FCSTD DOCUMENT  (FreeCAD 0.18R4 (GitTag))
Label: commutationSystem1
License: All rights reserved
LicenseURL: http://en.wikipedia.org/wiki/All_rights_reserved
objects: Sketcher::SketchObject×5, PartDesign::Body×2, Spreadsheet::Sheet×1
note: 7 computed .brp shape members not serialized (recipe doc carries the construction recipe); baked Part::Feature solids carry a one-line shape summary decoded from their .brp

FEATURE [Spreadsheet::Sheet] Spreadsheet  label="Variables"
  cells = A2=segmentNumber; B2(segmentNumber)=6; A3=outerDiameter; B3(outerDiameter)=30; D3=Calc Value; A4=innerDiameter; B4(innerDiameter)=24.7; D4=Input Value; A5=length; B5(length)=5; A6=segmentAngle; B6(segmentAngle)==360 / segmentNumber; A7=brushWidth; B7(brushWidth)=6; A8=brushHeight; B8(brushHeight)=2; A9=brushLength; B9(brushLength)=5; A10=commutatorDisplacementAngle; B10(commutatorDisplacementAngle)=6; A11=statorStackLength; B11(statorStackLength)=20; A12=stackDistance; B12(stackDistance)=10; A13=commutatorIsolationThickness; B13(commutatorIsolationThickness)=0.5
FEATURE [Sketcher::SketchObject] Sketch003  label="CommutatorSegment"
  MapMode = 5
  expr: Constraints[20] = Variables.commutatorIsolationThickness / 2
  expr: Constraints[13] = Variables.segmentAngle / 2 + Variables.commutatorDisplacementAngle
  expr: Constraints[12] = Variables.segmentAngle
  expr: Constraints[3] = Variables.outerDiameter
  expr: Placement.Rotation.Angle = 0
  expr: Constraints[2] = Variables.innerDiameter
  sketch-geometry (12):
    g0: Circle [constr] CenterX=0 CenterY=0 CenterZ=0 NormalX=0 NormalY=0 NormalZ=1 AngleXU=0 Radius=12.35
    g1: Circle [constr] CenterX=0 CenterY=0 CenterZ=0 NormalX=0 NormalY=0 NormalZ=1 AngleXU=0 Radius=15
    g2: LineSegment [constr] StartX=11.2823 StartY=-5.0232 StartZ=0 EndX=13.7032 EndY=-6.10105 EndZ=0
    g3: LineSegment [constr] StartX=9.99136 StartY=7.25915 StartZ=0 EndX=12.1353 EndY=8.81678 EndZ=0
    g4: LineSegment [constr] StartX=0 StartY=0 StartZ=0 EndX=11.2823 EndY=-5.0232 EndZ=0
    g5: LineSegment [constr] StartX=0 StartY=0 StartZ=0 EndX=9.99136 EndY=7.25915 EndZ=0
    g6: LineSegment StartX=10.1363 StartY=7.05541 StartZ=0 EndX=12.2805 EndY=8.6133 EndZ=0
    g7: LineSegment [constr] StartX=9.98931 StartY=7.25766 StartZ=0 EndX=10.1363 EndY=7.05541 EndZ=0
    g8: LineSegment StartX=11.3817 StartY=-4.79378 StartZ=0 EndX=13.803 EndY=-5.87182 EndZ=0
    g9: LineSegment [constr] StartX=11.3817 StartY=-4.79378 StartZ=0 EndX=11.28 EndY=-5.02217 EndZ=0
    g10: ArcOfCircle CenterX=0 CenterY=0 CenterZ=0 NormalX=0 NormalY=0 NormalZ=1 AngleXU=0 Radius=12.35 StartAngle=5.88455 EndAngle=6.89126
    g11: ArcOfCircle CenterX=0 CenterY=0 CenterZ=0 NormalX=0 NormalY=0 NormalZ=1 AngleXU=0 Radius=15 StartAngle=5.88097 EndAngle=6.89484
  constraints (34):
    c: Coincident(g0,g-1)
    c: Coincident(g1,g0)
    c: Diameter(g0) = 24.7
    c: Diameter(g1) = 30
    c: PointOnObject(g2,g0)
    c: PointOnObject(g2,g1)
    c: Coincident(g4,g-1)
    c: Coincident(g4,g2)
    c: Coincident(g5,g4)
    c: Coincident(g5,g3)
    c: Parallel(g4,g2)
    c: Parallel(g5,g3)
    c: Angle(g4,g5) = 1.0472
    c: Angle(g-1,g5) = 0.628319
    c: PointOnObject(g3,g1)
    c: PointOnObject(g3,g0)
    c: Parallel(g3,g6)
    c: PointOnObject(g7,g3)
    c: Coincident(g7,g6)
    c: Angle(g6,g7) = 1.5708
    c: Distance(g7) = 0.25
    c: PointOnObject(g8,g0)
    c: Parallel(g8,g2)
    c: Coincident(g9,g8)
    c: PointOnObject(g9,g4)
    c: Angle(g9,g8) = 1.5708
    c: Equal(g9,g7)
    c: PointOnObject(g8,g1)
    c: Coincident(g10,g-1)
    c: Coincident(g10,g8)
    c: Coincident(g10,g6)
    c: Coincident(g11,g10)
    c: Coincident(g11,g8)
    c: Coincident(g11,g6)
FEATURE [Sketcher::SketchObject] Sketch  label="BoundingBox"
  MapMode = 5
  Support = -> [XY_Plane]
  expr: Constraints[8] = Variables.outerDiameter
  sketch-geometry (6):
    g0: LineSegment StartX=-15 StartY=-15 StartZ=0 EndX=15 EndY=-15 EndZ=0
    g1: LineSegment StartX=15 StartY=-15 StartZ=0 EndX=15 EndY=15 EndZ=0
    g2: LineSegment StartX=15 StartY=15 StartZ=0 EndX=-15 EndY=15 EndZ=0
    g3: LineSegment StartX=-15 StartY=15 StartZ=0 EndX=-15 EndY=-15 EndZ=0
    g4: LineSegment [constr] StartX=-15 StartY=-15 StartZ=0 EndX=15 EndY=15 EndZ=0
    g5: GeomPoint X=0 Y=0 Z=0
  constraints (14):
    c: Coincident(g0,g1)
    c: Coincident(g1,g2)
    c: Coincident(g2,g3)
    c: Coincident(g3,g0)
    c: Horizontal(g0)
    c: Horizontal(g2)
    c: Vertical(g1)
    c: Vertical(g3)
    c: DistanceY(g1,g1) = 30
    c: Equal(g2,g1)
    c: Coincident(g4,g0)
    c: Coincident(g4,g1)
    c: Symmetric(g0,g1,g5)
    c: Coincident(g-1,g5)
FEATURE [Sketcher::SketchObject] Sketch004  label="BrushTop"
  MapMode = 5
  Support = -> [XY_Plane]
  expr: Constraints[10] = Variables.outerDiameter / 2
  expr: Constraints[8] = Variables.brushLength
  expr: Constraints[6] = Variables.brushWidth
  sketch-geometry (4):
    g0: ArcOfCircle CenterX=0 CenterY=0 CenterZ=0 NormalX=0 NormalY=0 NormalZ=1 AngleXU=0 Radius=15 StartAngle=6.08183 EndAngle=6.48454
    g1: LineSegment StartX=14.6969 StartY=3 StartZ=0 EndX=19.6969 EndY=3 EndZ=0
    g2: LineSegment StartX=19.6969 StartY=3 StartZ=0 EndX=19.6969 EndY=-3 EndZ=0
    g3: LineSegment StartX=19.6969 StartY=-3 StartZ=0 EndX=14.6969 EndY=-3 EndZ=0
  constraints (11):
    c: Coincident(g0,g-1)
    c: Coincident(g1,g0)
    c: Horizontal(g1)
    c: Coincident(g2,g1)
    c: Coincident(g3,g0)
    c: Horizontal(g3)
    c: DistanceY(g2,g2) = 6
    c: Coincident(g3,g2)
    c: DistanceX(g1,g1) = 5
    c: Symmetric(g1,g2,g-1)
    c: Radius(g0) = 15
FEATURE [PartDesign::Body] Body  label="TopView"
  Group = -> [Sketch003,Sketch,Sketch004]
  Origin = -> Origin
FEATURE [Sketcher::SketchObject] Sketch005  label="CommutatorSide"
  MapMode = 5
  Support = -> [XY_Plane001]
  expr: Constraints[22] = Variables.innerDiameter
  expr: Constraints[21] = Variables.outerDiameter
  expr: Constraints[20] = Variables.length
  expr: Constraints[19] = Variables.statorStackLength / 2 + Variables.stackDistance
  sketch-geometry (8):
    g0: LineSegment StartX=-25 StartY=15 StartZ=0 EndX=-20 EndY=15 EndZ=0
    g1: LineSegment StartX=-20 StartY=15 StartZ=0 EndX=-20 EndY=12.35 EndZ=0
    g2: LineSegment StartX=-20 StartY=12.35 StartZ=0 EndX=-25 EndY=12.35 EndZ=0
    g3: LineSegment StartX=-25 StartY=12.35 StartZ=0 EndX=-25 EndY=15 EndZ=0
    g4: LineSegment StartX=-25 StartY=-12.35 StartZ=0 EndX=-20 EndY=-12.35 EndZ=0
    g5: LineSegment StartX=-20 StartY=-12.35 StartZ=0 EndX=-20 EndY=-15 EndZ=0
    g6: LineSegment StartX=-20 StartY=-15 StartZ=0 EndX=-25 EndY=-15 EndZ=0
    g7: LineSegment StartX=-25 StartY=-15 StartZ=0 EndX=-25 EndY=-12.35 EndZ=0
  constraints (23):
    c: Coincident(g0,g1)
    c: Coincident(g1,g2)
    c: Coincident(g2,g3)
    c: Coincident(g3,g0)
    c: Horizontal(g0)
    c: Vertical(g1)
    c: Vertical(g3)
    c: Coincident(g4,g5)
    c: Coincident(g5,g6)
    c: Coincident(g6,g7)
    c: Coincident(g7,g4)
    c: Horizontal(g6)
    c: Vertical(g5)
    c: Vertical(g7)
    c: Equal(g4,g2)
    c: Equal(g7,g3)
    c: Symmetric(g4,g2,g-1)
    c: Horizontal(g4)
    c: Horizontal(g2)
    c: DistanceX(g1,g-1) = 20
    c: DistanceX(g0,g0) = 5
    c: DistanceY(g6,g0) = 30
    c: DistanceY(g4,g2) = 24.7
FEATURE [Sketcher::SketchObject] Sketch006  label="BrushesSide"
  MapMode = 5
  Support = -> [XY_Plane001]
  expr: Constraints[22] = Variables.outerDiameter / 2
  expr: Constraints[19] = Variables.outerDiameter
  expr: Constraints[20] = Variables.statorStackLength / 2 + Variables.stackDistance + Variables.length / 2 - Variables.brushHeight / 2
  expr: Constraints[15] = Variables.brushLength
  expr: Constraints[21] = Variables.statorStackLength / 2 + Variables.stackDistance + Variables.length / 2 - Variables.brushHeight / 2
  expr: Constraints[16] = Variables.brushHeight
  sketch-geometry (8):
    g0: LineSegment StartX=-23.5 StartY=20 StartZ=0 EndX=-21.5 EndY=20 EndZ=0
    g1: LineSegment StartX=-21.5 StartY=20 StartZ=0 EndX=-21.5 EndY=15 EndZ=0
    g2: LineSegment StartX=-21.5 StartY=15 StartZ=0 EndX=-23.5 EndY=15 EndZ=0
    g3: LineSegment StartX=-23.5 StartY=15 StartZ=0 EndX=-23.5 EndY=20 EndZ=0
    g4: LineSegment StartX=-23.5 StartY=-20 StartZ=0 EndX=-21.5 EndY=-20 EndZ=0
    g5: LineSegment StartX=-21.5 StartY=-20 StartZ=0 EndX=-21.5 EndY=-15 EndZ=0
    g6: LineSegment StartX=-21.5 StartY=-15 StartZ=0 EndX=-23.5 EndY=-15 EndZ=0
    g7: LineSegment StartX=-23.5 StartY=-15 StartZ=0 EndX=-23.5 EndY=-20 EndZ=0
  constraints (24):
    c: Coincident(g0,g1)
    c: Coincident(g1,g2)
    c: Coincident(g2,g3)
    c: Coincident(g3,g0)
    c: Horizontal(g0)
    c: Horizontal(g2)
    c: Vertical(g3)
    c: Coincident(g4,g5)
    c: Coincident(g5,g6)
    c: Coincident(g6,g7)
    c: Coincident(g7,g4)
    c: Horizontal(g6)
    c: Vertical(g7)
    c: Equal(g2,g6)
    c: Equal(g3,g7)
    c: DistanceY(g3,g3) = 5
    c: DistanceX(g0,g0) = 2
    c: Vertical(g5)
    c: Vertical(g1)
    c: DistanceY(g6,g2) = 30
    c: DistanceX(g1,g-1) = 21.5
    c: DistanceX(g5,g-1) = 21.5
    c: DistanceY(g-1,g2) = 15
    c: Angle(g5,g4) = 1.5708
FEATURE [PartDesign::Body] Body001  label="SideView"
  Group = -> [Sketch005,Sketch006]
  Origin = -> Origin001
